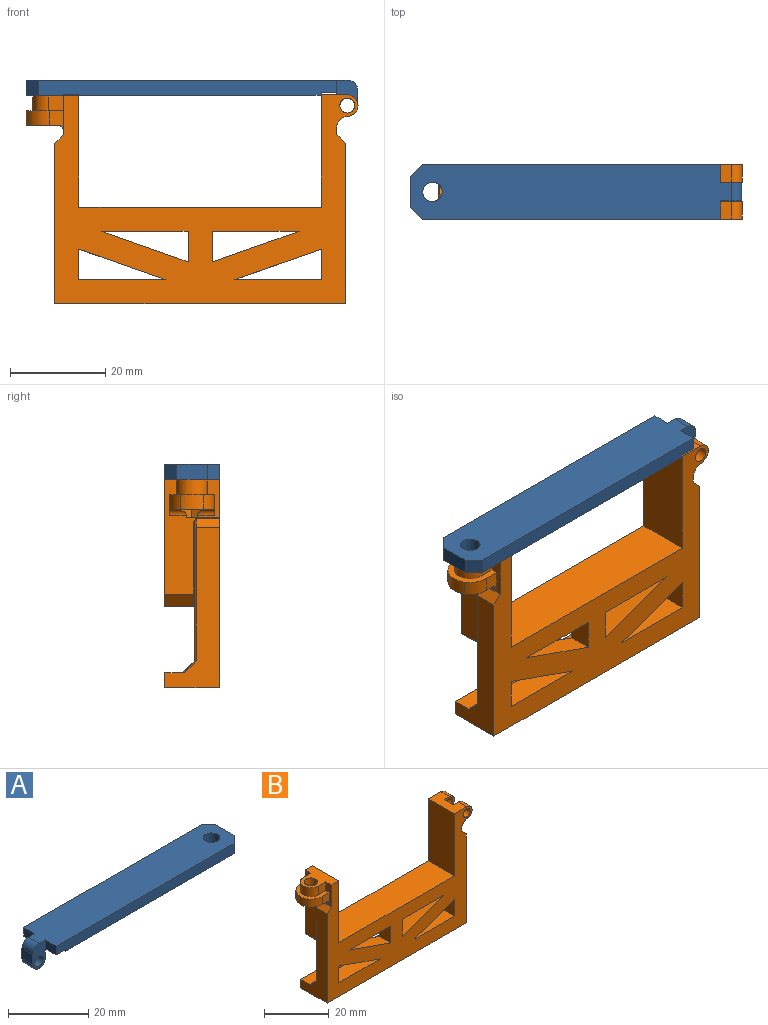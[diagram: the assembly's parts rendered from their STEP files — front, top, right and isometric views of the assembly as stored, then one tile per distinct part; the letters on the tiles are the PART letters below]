
ASSEMBLY  parts=2 mates=1
PART A: 19 faces, bbox 69.5x11.4x7.6 mm
  f0: plane 3.81x2.71mm, normal (1,0,0), area 10.3mm2, adj f4,f7,f11,f13
  f1: plane 3.81x3.13mm, normal (-1,0,0), area 11.9mm2, adj f3,f4,f11,f13
  f2: plane 67.27x11.43mm, normal (0,0,1), area 732.9mm2, adj f3,f5,f6,f10,f11,f12,f13,f14
  f3: cylinder r=2.25mm len=3.81mm, axis (0,1,0), area 13.5mm2, adj f1,f2,f11,f13
  f4: cylinder r=2.2mm len=4.4mm, axis (0,1,0), area 26.3mm2, adj f0,f1,f11,f13
  f5: plane 62.58x3.18mm, normal (0,-1,0), area 197mm2, adj f2,f7,f8,f9,f14,f18
  f6: plane 62.58x3.18mm, normal (0,1,0), area 197mm2, adj f2,f7,f8,f9,f12,f17
  f7: plane 11.43x3.3mm, normal (0,0,-1), area 37.7mm2, adj f0,f5,f6,f8,f12,f14
  f8: plane 11.43x0.51mm, normal (-1,0,0), area 5.8mm2, adj f5,f6,f7,f9
  f9: plane 61.82x11.43mm, normal (0,0,-1), area 687mm2, adj f5,f6,f8,f10,f16,f17,f18
  f10: plane 6.35x3.18mm, normal (1,0,0), area 20.2mm2, adj f2,f9,f17,f18
  f11: plane 7.58x4.4mm, normal (0,1,0), area 22.6mm2, adj f0,f1,f2,f3,f4,f12,f15
  f12: plane 3.81x2.67mm, normal (-1,0,0), area 10.2mm2, adj f2,f6,f7,f11
  f13: plane 7.58x4.4mm, normal (0,-1,0), area 22.6mm2, adj f0,f1,f2,f3,f4,f14,f15
  f14: plane 3.81x2.67mm, normal (-1,0,0), area 10.2mm2, adj f2,f5,f7,f13
  f15: cylinder r=1.55mm len=3.81mm, axis (0,1,0), area 37.1mm2, adj f11,f13
  f16: cylinder r=2.05mm len=4.1mm, axis (0,0,1), area 40.9mm2, adj f2,f9
  f17: plane 3.18x2.54mm, normal (0.71,0.71,0), area 11.4mm2, adj f2,f6,f9,f10
  f18: plane 3.18x2.54mm, normal (0.71,-0.71,0), area 11.4mm2, adj f2,f5,f9,f10
PART B: 100 faces, bbox 69.5x11.4x43.8 mm
  f0: plane 24.13x11.43mm, normal (-1,0,0), area 127.7mm2, adj f3,f5,f11,f12,f39,f56,f57,f59
  f1: cylinder r=2.05mm len=4.1mm, axis (0,0,1), area 49.1mm2, adj f78,f87
  f2: plane 9.37x6.61mm, normal (0,0,-1), area 18.7mm2, adj f84,f85,f88,f89,f90,f91,f92,f93
  f3: plane 3.3x3.23mm, normal (0.01,1,0), area 10.7mm2, adj f0,f4,f78,f86
  f4: cylinder r=3.25mm len=6.5mm, axis (0,0,1), area 33.8mm2, adj f3,f5,f78,f86
  f5: plane 3.3x3.25mm, normal (0,-1,0), area 10.7mm2, adj f0,f4,f78,f86
  f6: plane 11.43x5.43mm, normal (0,0,1), area 52.9mm2, adj f8,f10,f11,f12,f20,f80,f82,f83
  f7: cylinder r=1.55mm len=3.68mm, axis (0,1,0), area 35.9mm2, adj f12,f83
  f8: cylinder r=2.25mm len=4.5mm, axis (0,1,0), area 25.5mm2, adj f6,f9,f12,f83
  f9: cylinder r=2.54mm len=3.68mm, axis (0,1,0), area 14.1mm2, adj f8,f10,f12,f83
  f10: plane 24.13x11.43mm, normal (1,0,0), area 139mm2, adj f6,f9,f11,f12,f38,f41,f44,f46
  f11: plane 63.56x43.82mm, normal (0,-1,0), area 1220.7mm2, adj f0,f6,f10,f14,f15,f16,f17,f18
  f12: plane 61.65x26.67mm, normal (0,1,0), area 336.1mm2, adj f0,f6,f7,f8,f9,f10,f20,f21
  f13: plane 60.45x29.13mm, normal (0,1,0), area 481.6mm2, adj f40,f43,f46,f48,f49,f51,f52,f53
  f14: plane 18.21x6.41mm, normal (-0.33,0,0.94), area 93.2mm2, adj f11,f15,f31,f77
  f15: plane 6.41x4.83mm, normal (1,0,0), area 30.9mm2, adj f11,f14,f31,f76
  f16: plane 19.74x5.72mm, normal (0,0,1), area 104.5mm2, adj f11,f17,f27,f35,f47,f54
  f17: plane 18.21x6.41mm, normal (0.33,0,-0.94), area 93.4mm2, adj f11,f16,f27,f54,f55,f58
  f18: plane 60.96x11.43mm, normal (0,0,-1), area 696.8mm2, adj f11,f19,f28,f34
  f19: plane 33.66x11.43mm, normal (1,0,0), area 186.4mm2, adj f11,f18,f33,f34,f37,f42,f43,f45
  f20: plane 23.5x11.43mm, normal (-1,0,0), area 268.5mm2, adj f6,f11,f12,f21
  f21: plane 50.8x11.43mm, normal (0,0,1), area 580.6mm2, adj f11,f12,f20,f22
  f22: plane 23.5x11.43mm, normal (1,0,0), area 268.5mm2, adj f11,f12,f21,f78
  f23: plane 6.41x5.36mm, normal (1,0,0), area 31.1mm2, adj f11,f24,f29,f68,f70,f71
  f24: plane 18.21x6.41mm, normal (-0.33,0,-0.94), area 93.4mm2, adj f11,f23,f29,f60,f63,f66
  f25: plane 6.41x4.83mm, normal (-1,0,0), area 30.9mm2, adj f11,f26,f30,f73
  f26: plane 18.21x6.41mm, normal (0.33,0,0.94), area 93.2mm2, adj f11,f25,f30,f74
  f27: plane 6.41x5.36mm, normal (-1,0,0), area 31.1mm2, adj f11,f16,f17,f47,f50,f52
  f28: plane 33.66x11.43mm, normal (-1,0,0), area 186.4mm2, adj f11,f18,f33,f34,f36,f64,f65,f67
  f29: plane 19.74x5.72mm, normal (0,0,1), area 104.5mm2, adj f11,f23,f24,f35,f60,f71
  f30: plane 18.21x4.83mm, normal (0,0,-1), area 87.9mm2, adj f11,f25,f26,f72
  f31: plane 18.21x4.83mm, normal (0,0,-1), area 87.9mm2, adj f11,f14,f15,f75
  f32: plane 52.07x6.1mm, normal (0,0,-1), area 317.4mm2, adj f12,f38,f39,f51
  f33: plane 60.96x4.17mm, normal (0,0,1), area 232.3mm2, adj f19,f28,f34,f35,f42,f65
  f34: plane 60.96x3.18mm, normal (0,1,0), area 193.5mm2, adj f18,f19,f28,f33
  f35: plane 60.45x2.47mm, normal (0,0.71,0.71), area 180.7mm2, adj f16,f29,f33,f42,f47,f48,f54,f60
  f36: plane 4.83x1.83mm, normal (-0.71,0,0.71), area 12.5mm2, adj f11,f28,f57,f62
  f37: plane 4.83x1.83mm, normal (0.71,0,0.71), area 12.5mm2, adj f11,f19,f40,f41
  f38: plane 6.1x2.54mm, normal (0.71,0,-0.71), area 21.9mm2, adj f10,f12,f32,f49
  f39: plane 6.1x2.54mm, normal (-0.71,0,-0.71), area 21.9mm2, adj f0,f12,f32,f53
  f40: plane 1.94x1.83mm, normal (0.5,0.71,0.5), area 0.8mm2, adj f13,f37,f43,f44
  f41: plane 4.83x0.18mm, normal (0.92,0,0.38), area 0.9mm2, adj f10,f11,f37,f44
  f42: plane 2.65x2.47mm, normal (0.71,0.5,0.5), area 1.2mm2, adj f19,f33,f35,f45
  f43: plane 27.83x0.25mm, normal (0.71,0.71,0), area 10mm2, adj f13,f19,f40,f45
  f44: bspline ~0.72x0.51mm, area 0.2mm2, adj f10,f40,f41,f46
  f45: plane 0.36x0.33mm, normal (0.68,0.68,0.28), area 0.1mm2, adj f19,f42,f43,f48
  f46: plane 15.37x0.25mm, normal (0.71,0.71,0), area 5.5mm2, adj f10,f13,f44,f49
  f47: plane 0.74x0.56mm, normal (-0.71,0.5,0.5), area 0.2mm2, adj f16,f27,f35,f50
  f48: plane 4.57x0.18mm, normal (0,0.92,0.38), area 0.9mm2, adj f13,f35,f45,f50
  f49: plane 2.79x2.79mm, normal (0.5,0.71,-0.5), area 1.3mm2, adj f13,f38,f46,f51
  f50: plane 0.36x0.33mm, normal (-0.68,0.68,0.28), area 0.1mm2, adj f27,f47,f48,f52
  f51: plane 52.28x0.25mm, normal (0,0.71,-0.71), area 18.7mm2, adj f13,f32,f49,f53
  f52: plane 6.03x0.25mm, normal (-0.71,0.71,0), area 2.1mm2, adj f13,f27,f50,f55
  f53: plane 2.79x2.79mm, normal (-0.5,0.71,-0.5), area 1.3mm2, adj f13,f39,f51,f56
  f54: plane 1.68x0.74mm, normal (0.41,0.87,-0.29), area 0.5mm2, adj f16,f17,f35,f58
  f55: plane 17.13x6.27mm, normal (0.23,0.71,-0.67), area 6.5mm2, adj f13,f17,f52,f58
  f56: plane 15.37x0.25mm, normal (-0.71,0.71,0), area 5.5mm2, adj f0,f13,f53,f59
  f57: plane 4.83x0.18mm, normal (-0.92,0,0.38), area 0.9mm2, adj f0,f11,f36,f59
  f58: bspline ~1.11x0.6mm, area 0.4mm2, adj f17,f54,f55,f61
  f59: bspline ~0.72x0.51mm, area 0.2mm2, adj f0,f56,f57,f62
  f60: plane 1.68x0.74mm, normal (-0.41,0.87,-0.29), area 0.5mm2, adj f24,f29,f35,f63
  f61: plane 17.05x0.18mm, normal (0,0.92,0.38), area 3.1mm2, adj f13,f35,f58,f63
  f62: plane 1.94x1.83mm, normal (-0.5,0.71,0.5), area 0.8mm2, adj f13,f36,f59,f64
  f63: bspline ~1.11x0.6mm, area 0.4mm2, adj f24,f60,f61,f66
  f64: plane 27.83x0.25mm, normal (-0.71,0.71,0), area 10mm2, adj f13,f28,f62,f67
  f65: plane 2.65x2.47mm, normal (-0.71,0.5,0.5), area 1.2mm2, adj f28,f33,f35,f67
  f66: plane 17.13x6.27mm, normal (-0.23,0.71,-0.67), area 6.5mm2, adj f13,f24,f63,f68
  f67: plane 0.36x0.33mm, normal (-0.68,0.68,0.28), area 0.1mm2, adj f28,f64,f65,f69
  f68: plane 6.03x0.25mm, normal (0.71,0.71,0), area 2.1mm2, adj f13,f23,f66,f70
  f69: plane 4.57x0.18mm, normal (0,0.92,0.38), area 0.9mm2, adj f13,f35,f67,f70
  f70: plane 0.36x0.33mm, normal (0.68,0.68,0.28), area 0.1mm2, adj f23,f68,f69,f71
  f71: plane 0.74x0.56mm, normal (0.71,0.5,0.5), area 0.2mm2, adj f23,f29,f35,f70
  f72: plane 19.95x0.25mm, normal (0,0.71,-0.71), area 6.9mm2, adj f13,f30,f73,f74
  f73: plane 7.02x0.25mm, normal (-0.71,0.71,0), area 2.4mm2, adj f13,f25,f72,f74
  f74: plane 19.95x7.02mm, normal (0.23,0.71,0.67), area 7.3mm2, adj f13,f26,f72,f73
  f75: plane 19.95x0.25mm, normal (0,0.71,-0.71), area 6.9mm2, adj f13,f31,f76,f77
  f76: plane 7.02x0.25mm, normal (0.71,0.71,0), area 2.4mm2, adj f13,f15,f75,f77
  f77: plane 19.95x7.02mm, normal (-0.23,0.71,0.67), area 7.3mm2, adj f13,f14,f75,f76
  f78: plane 11.43x9.68mm, normal (0,0,1), area 60.8mm2, adj f0,f1,f3,f4,f5,f11,f12,f22
  f79: cylinder r=1.55mm len=3.68mm, axis (0,1,0), area 35.9mm2, adj f11,f82
  f80: cylinder r=2.25mm len=4.5mm, axis (0,1,0), area 25.5mm2, adj f6,f11,f81,f82
  f81: cylinder r=2.54mm len=3.68mm, axis (0,1,0), area 14.1mm2, adj f10,f11,f80,f82
  f82: plane 7.03x4.5mm, normal (0,1,0), area 11.9mm2, adj f6,f10,f79,f80,f81
  f83: plane 7.03x4.5mm, normal (0,-1,0), area 11.9mm2, adj f6,f7,f8,f9,f10
  f84: plane 4.32x3.02mm, normal (0,-1,0), area 9.6mm2, adj f0,f2,f86,f95,f99
  f85: plane 4.32x3.02mm, normal (0,1,0), area 9.6mm2, adj f0,f2,f86,f96,f97
  f86: plane 9.37x7.88mm, normal (0,0,1), area 26.7mm2, adj f0,f3,f4,f5,f84,f85,f97,f98
  f87: plane 7.89x6.83mm, normal (0,0,-1), area 27.2mm2, adj f1,f88,f89,f90,f91,f92,f93
  f88: plane 4.32x3.42mm, normal (-0.87,0.5,0), area 13.2mm2, adj f0,f2,f87,f89,f93,f94,f95
  f89: plane 3.95x2.54mm, normal (0,1,0), area 10mm2, adj f2,f87,f88,f90
  f90: plane 3.42x2.54mm, normal (0.87,0.5,0), area 10mm2, adj f2,f87,f89,f91
  f91: plane 3.42x2.54mm, normal (0.87,-0.5,0), area 10mm2, adj f2,f87,f90,f92
  f92: plane 3.95x2.54mm, normal (0,-1,0), area 10mm2, adj f2,f87,f91,f93
  f93: plane 4.32x3.42mm, normal (-0.87,-0.5,0), area 13.2mm2, adj f0,f2,f87,f88,f92,f94,f96
  f94: plane 2.41x0.7mm, normal (0,0,1), area 0.8mm2, adj f0,f88,f93
  f95: cylinder r=1.27mm len=3.48mm, axis (0,1,0), area 5.4mm2, adj f0,f2,f84,f88
  f96: cylinder r=1.27mm len=3.48mm, axis (0,1,0), area 5.4mm2, adj f0,f2,f85,f93
  f97: cylinder r=5.08mm len=4.28mm, axis (0,0,-1), area 15.5mm2, adj f2,f85,f86,f98
  f98: cylinder r=5.08mm len=4.68mm, axis (0,0,-1), area 14.8mm2, adj f2,f86,f97,f99
  f99: cylinder r=5.08mm len=4.28mm, axis (0,0,1), area 15.5mm2, adj f2,f84,f86,f98
PLACE A rot(axis=(0,0,1),180deg) t=(-12.85,-10.71,37.41)mm
PLACE B t=(-28.45,-5.61,-4.15)mm
MATE slider A.f4 <-> B.f7  axis (0,-1,0) through (2.38,-3.09,37.41)mm
